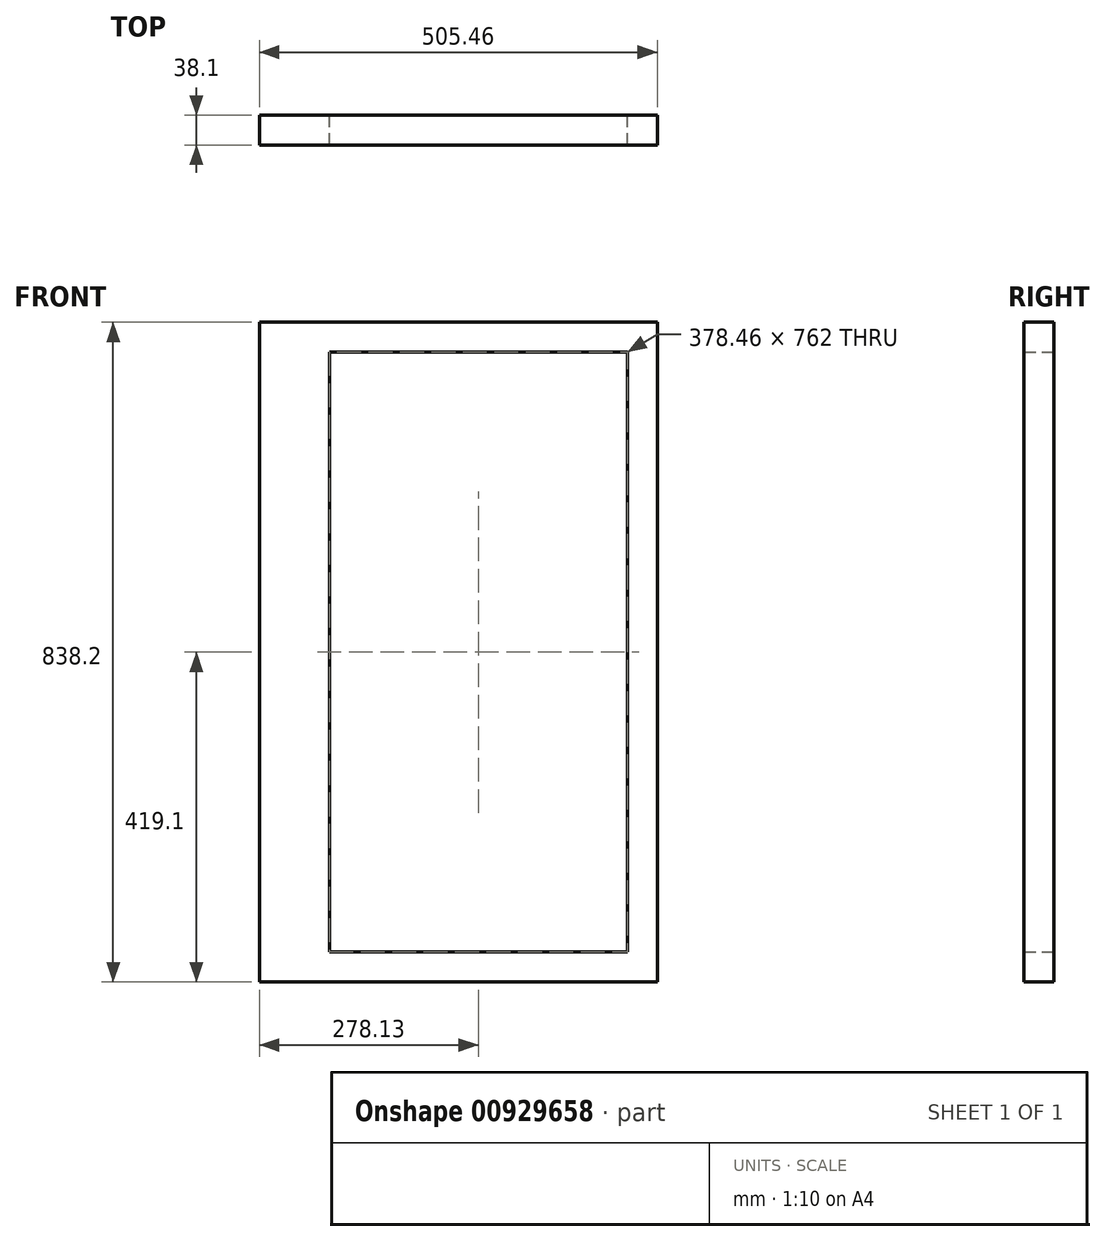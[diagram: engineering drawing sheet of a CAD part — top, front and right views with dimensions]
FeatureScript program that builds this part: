
annotation { "Feature Type Name" : "Feature", "Feature Type Description" : "" }
export const myFeature = defineFeature(function(context is Context, id is Id, definition is map)
    precondition{}
    {
        {
            var Q0;
            Q0=qCreatedBy(makeId("Front.planeOp"),FACE);
            var sketch = newSketch(context, id + "F0", { "sketchPlane" : qUnion([Q0])});
            skLineSegment(sketch, "E0.bottom", {"start": v(-44.45, -381) * mm, "end": v(44.45, -381) * mm});
            skLineSegment(sketch, "E0.top", {"start": v(-44.45, 381) * mm, "end": v(44.45, 381) * mm});
            skLineSegment(sketch, "E0.left", {"start": v(-44.45, -381) * mm, "end": v(-44.45, 381) * mm});
            skLineSegment(sketch, "E0.right", {"start": v(44.45, -381) * mm, "end": v(44.45, 381) * mm});
            skPoint(sketch, "E0.middle", {"position": v(0, 0) * mm});
            skSolve(sketch);
        }
        {
            var Q0;
            Q0=qSketchRegion(id+"F0",true);
            extrude(context, id + "F1", {"entities" : qUnion([Q0]), "depth" : 38.1 * mm, "offsetDistance" : 25.4 * mm});
        }
        {
            var Q0;
            Q0=qCreatedBy(makeId("Front.planeOp"),FACE);
            var sketch = newSketch(context, id + "F2", { "sketchPlane" : qUnion([Q0])});
            skLineSegment(sketch, "E1.bottom", {"start": v(-44.45, 381) * mm, "end": v(461, 381) * mm});
            skLineSegment(sketch, "E1.top", {"start": v(-44.45, 419.1) * mm, "end": v(461, 419.1) * mm});
            skLineSegment(sketch, "E1.left", {"start": v(-44.45, 381) * mm, "end": v(-44.45, 419.1) * mm});
            skLineSegment(sketch, "E1.right", {"start": v(461, 381) * mm, "end": v(461, 419.1) * mm});
            skSolve(sketch);
        }
        {
            var Q0;
            Q0=makeQuery(id+"F2.imprint","IMPRINT",FACE,{"disambiguationData":[TD([[makeQuery(id+"F2.imprint","IMPRINT",EDGE,{"derivedFrom":sQuery(id+"F2.wireOp",EDGE,"E1.bottom")}),1.0]])]});
            extrude(context, id + "F3", {"entities" : qUnion([Q0]), "operationType" : NewBodyOperationType.ADD, "depth" : 38.1 * mm, "offsetDistance" : 25.4 * mm});
        }
        {
            var Q0;
            Q0=qCreatedBy(makeId("Front.planeOp"),FACE);
            var sketch = newSketch(context, id + "F4", { "sketchPlane" : qUnion([Q0])});
            skLineSegment(sketch, "E2.bottom", {"start": v(422.9, -381) * mm, "end": v(461.01, -381) * mm});
            skLineSegment(sketch, "E2.top", {"start": v(422.9, 381) * mm, "end": v(461, 381) * mm});
            skLineSegment(sketch, "E2.left", {"start": v(422.9, -381) * mm, "end": v(422.9, 381) * mm});
            skLineSegment(sketch, "E2.right", {"start": v(461.01, -381) * mm, "end": v(461, 381) * mm});
            skPoint(sketch, "E2.middle", {"position": v(441.96, 0) * mm});
            skSolve(sketch);
        }
        {
            var Q0;
            Q0=makeQuery(id+"F4.imprint","IMPRINT",FACE,{"disambiguationData":[TD([[makeQuery(id+"F4.imprint","IMPRINT",EDGE,{"derivedFrom":sQuery(id+"F4.wireOp",EDGE,"E2.bottom")}),1.0]])]});
            extrude(context, id + "F5", {"entities" : qUnion([Q0]), "operationType" : NewBodyOperationType.ADD, "depth" : 38.1 * mm, "offsetDistance" : 25.4 * mm});
        }
        {
            var Q0;
            Q0=qCreatedBy(makeId("Front.planeOp"),FACE);
            var sketch = newSketch(context, id + "F6", { "sketchPlane" : qUnion([Q0])});
            skLineSegment(sketch, "E3.bottom", {"start": v(-44.45, -419.1) * mm, "end": v(461.01, -419.1) * mm});
            skLineSegment(sketch, "E3.top", {"start": v(-44.45, -381) * mm, "end": v(461.01, -381) * mm});
            skLineSegment(sketch, "E3.left", {"start": v(-44.45, -419.1) * mm, "end": v(-44.45, -381) * mm});
            skLineSegment(sketch, "E3.right", {"start": v(461.01, -419.1) * mm, "end": v(461.01, -381) * mm});
            skSolve(sketch);
        }
        {
            var Q0;
            Q0=makeQuery(id+"F6.imprint","IMPRINT",FACE,{"disambiguationData":[TD([[makeQuery(id+"F6.imprint","IMPRINT",EDGE,{"derivedFrom":sQuery(id+"F6.wireOp",EDGE,"E3.bottom")}),1.0]])]});
            extrude(context, id + "F7", {"entities" : qUnion([Q0]), "operationType" : NewBodyOperationType.ADD, "depth" : 38.1 * mm, "offsetDistance" : 25.4 * mm});
        }
    });
